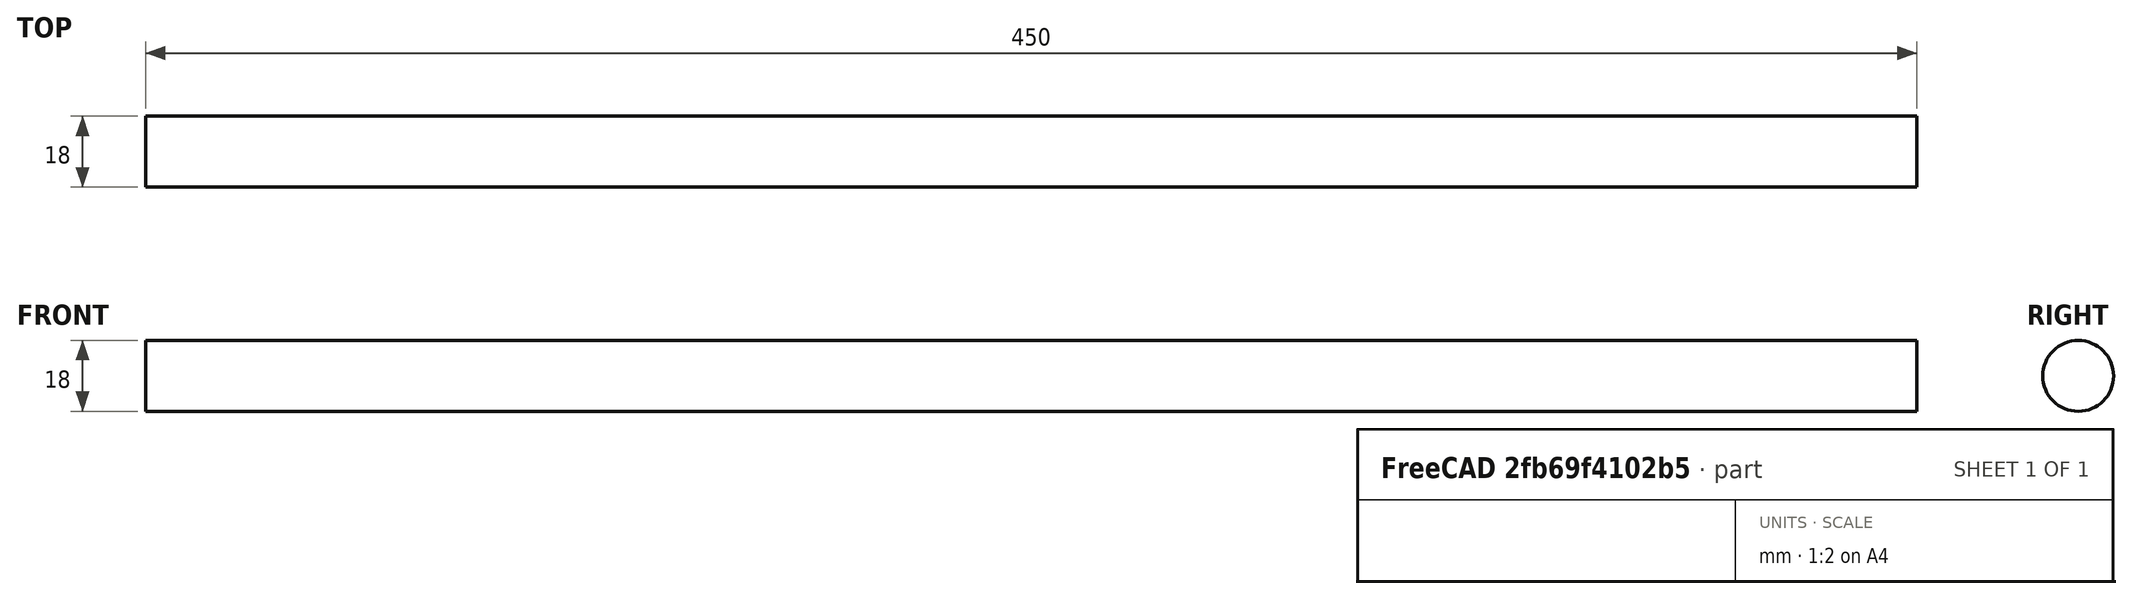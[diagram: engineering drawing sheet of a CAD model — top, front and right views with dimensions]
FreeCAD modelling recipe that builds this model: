
FCSTD DOCUMENT  (FreeCAD 0.19R18028 (Git))
Label: upper-stage-rod
License: Public Domain
LicenseURL: http://en.wikipedia.org/wiki/Public_domain
objects: Part::FeaturePython×5, App::FeaturePython×2, Sketcher::SketchObject×1, PartDesign::Pad×1, PartDesign::Body×1
note: 8 computed .brp shape members not serialized (recipe doc carries the construction recipe); baked Part::Feature solids carry a one-line shape summary decoded from their .brp

FEATURE [App::FeaturePython] Constraints  # WARN: FeaturePython — macro-defined, semantics opaque (R4)
  GroupMode = 1
  _Version = 1
FEATURE [Sketcher::SketchObject] Sketch
  MapMode = 5
  Placement = pos=(0,0,0) rot=(0.57735,0.57735,0.57735;2.0944rad)
  Support = -> [YZ_Plane]
  sketch-geometry (1):
    g0: Circle CenterX=0 CenterY=0 CenterZ=0 NormalX=0 NormalY=0 NormalZ=1 AngleXU=0 Radius=9
  constraints (2):
    c: Coincident(g0,g-1)
    c: Radius(g0) = 9
FEATURE [PartDesign::Pad] Pad
  ClaimChildren = false
  Length = 450
  Length2 = 100
  Midplane = true
  Placement = pos=(0,0,0) rot=(0.57735,0.57735,0.57735;2.0944rad)
  Profile = -> Sketch
  Type = 0
FEATURE [PartDesign::Body] Body
  Group = -> [Sketch,Pad]
  Origin = -> Origin
  Tip = -> Pad
FEATURE [Part::FeaturePython] Parts  # WARN: FeaturePython — macro-defined, semantics opaque (R4)
  Group = -> [Body]
  GroupMode = 0
FEATURE [Part::FeaturePython] Assembly  label="upper-stage-rod"  # WARN: FeaturePython — macro-defined, semantics opaque (R4)
  AutoRelax = true
  BuildShape = 0
  Freeze = false
  Group = -> [Constraints,Elements,Parts]
  GroupMode = 1
  SolverType = 1
  Verbose = false
  _SolverType = 1
  _Version = 1
FEATURE [App::FeaturePython] Elements  # WARN: FeaturePython — macro-defined, semantics opaque (R4)
  Group = -> [Element,Element001,Element002]
  GroupMode = 1
FEATURE [Part::FeaturePython] Element  label="middle"  # link proxy (typed FeaturePython)
  Detach = false
  LinkTransform = true
  LinkedObject = -> Body [Pad.Sketch.Edge1]
  _Parent = -> Elements
FEATURE [Part::FeaturePython] Element001  label="left"  # link proxy (typed FeaturePython)
  Detach = false
  LinkTransform = true
  LinkedObject = -> Body [Pad.Edge2]
  _Parent = -> Elements
FEATURE [Part::FeaturePython] Element002  label="right"  # link proxy (typed FeaturePython)
  Detach = false
  LinkTransform = true
  LinkedObject = -> Body [Pad.Edge3]
  _Parent = -> Elements
